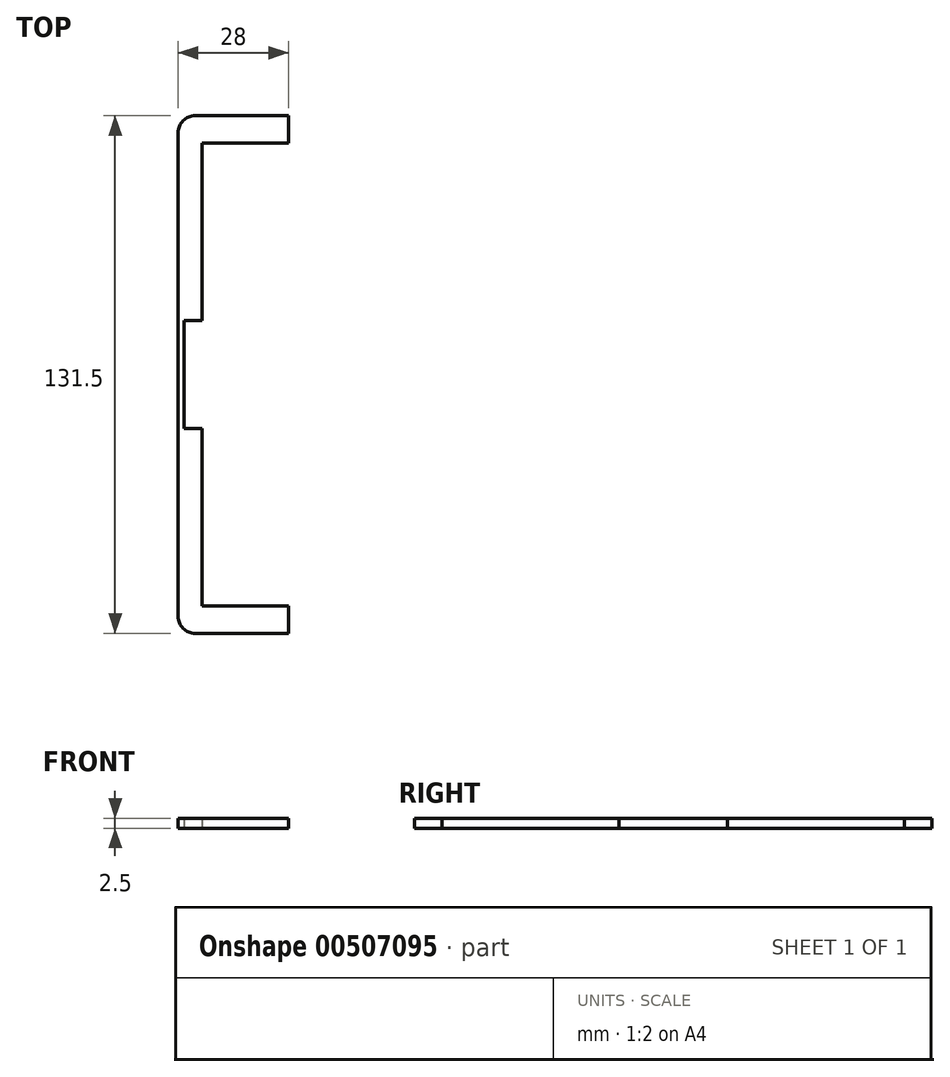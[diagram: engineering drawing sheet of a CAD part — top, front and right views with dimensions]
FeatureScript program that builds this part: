
annotation { "Feature Type Name" : "Feature", "Feature Type Description" : "" }
export const myFeature = defineFeature(function(context is Context, id is Id, definition is map)
    precondition{}
    {
        {
            var Q0;
            Q0=qCreatedBy(makeId("Top.planeOp"),FACE);
            var sketch = newSketch(context, id + "F0", { "sketchPlane" : qUnion([Q0])});
            skLineSegment(sketch, "E0", {"start": v(0, 58.75) * mm, "end": v(0, 65.75) * mm});
            skLineSegment(sketch, "E1", {"start": v(0, 65.75) * mm, "end": v(-23.68, 65.75) * mm});
            skLineSegment(sketch, "E2", {"start": v(-28, 61.43) * mm, "end": v(-28, -61.43) * mm});
            skLineSegment(sketch, "E3", {"start": v(-23.68, -65.75) * mm, "end": v(0, -65.75) * mm});
            skLineSegment(sketch, "E4", {"start": v(0, -65.75) * mm, "end": v(0, -58.75) * mm});
            skLineSegment(sketch, "E5", {"start": v(0, -58.75) * mm, "end": v(-22, -58.75) * mm});
            skLineSegment(sketch, "E6", {"start": v(-22, -58.75) * mm, "end": v(-22, -13.75) * mm});
            skLineSegment(sketch, "E7", {"start": v(-22, -13.75) * mm, "end": v(-26.5, -13.75) * mm});
            skLineSegment(sketch, "E8", {"start": v(-26.5, -13.75) * mm, "end": v(-26.5, 13.75) * mm});
            skLineSegment(sketch, "E9", {"start": v(-26.5, 13.75) * mm, "end": v(-22, 13.75) * mm});
            skLineSegment(sketch, "E10", {"start": v(-22, 13.75) * mm, "end": v(-22, 58.75) * mm});
            skLineSegment(sketch, "E11", {"start": v(-22, 58.75) * mm, "end": v(0, 58.75) * mm});
            skPoint(sketch, "E12.visualSharp", {"position": v(-28, 65.75) * mm});
            skArc(sketch, "E12.filletArc", {"start": v(-23.68, 65.75) * mm, "mid": v(-26.74, 64.49) * mm, "end": v(-28, 61.43) * mm});
            skPoint(sketch, "E13.visualSharp", {"position": v(-28, -65.75) * mm});
            skArc(sketch, "E13.filletArc", {"start": v(-28, -61.43) * mm, "mid": v(-26.74, -64.49) * mm, "end": v(-23.68, -65.75) * mm});
            skSolve(sketch);
        }
        {
            var Q0;
            Q0 = qSketchRegion(id + "F0", true);
            extrude(context, id + "F1", {"entities" : qUnion([Q0]), "depth" : 2.5 * mm});
        }
        {
            var Q0;
            Q0=makeQuery(id+"F1.opExtrude","CAP_FACE",FACE,{"disambiguationData":[OSD([sQuery(id+"F0.wireOp",EDGE,"E0"),sQuery(id+"F0.wireOp",EDGE,"E1"),sQuery(id+"F0.wireOp",EDGE,"E2"),sQuery(id+"F0.wireOp",EDGE,"E3"),sQuery(id+"F0.wireOp",EDGE,"E4"),sQuery(id+"F0.wireOp",EDGE,"E5"),sQuery(id+"F0.wireOp",EDGE,"E6"),sQuery(id+"F0.wireOp",EDGE,"E7"),sQuery(id+"F0.wireOp",EDGE,"E8"),sQuery(id+"F0.wireOp",EDGE,"E9"),sQuery(id+"F0.wireOp",EDGE,"E10"),sQuery(id+"F0.wireOp",EDGE,"E11"),sQuery(id+"F0.wireOp",EDGE,"E12.filletArc"),sQuery(id+"F0.wireOp",EDGE,"E13.filletArc")])],"isStart":false});
            var sketch = newSketch(context, id + "F2", { "sketchPlane" : qUnion([Q0])});
            skLineSegment(sketch, "E14.0", {"start": v(-22, 58.75) * mm, "end": v(0, 58.75) * mm});
            skLineSegment(sketch, "E15.0", {"start": v(-22, 13.75) * mm, "end": v(-22, 58.75) * mm});
            skLineSegment(sketch, "E16.0", {"start": v(-28, 61.43) * mm, "end": v(-28, -61.43) * mm});
            skLineSegment(sketch, "E17.0", {"start": v(-26.5, -13.75) * mm, "end": v(-26.5, 13.75) * mm});
            skPoint(sketch, "E18.0", {"position": v(-24.25, 13.75) * mm});
            skLineSegment(sketch, "E19.0", {"start": v(-26.5, 13.75) * mm, "end": v(-22, 13.75) * mm});
            skLineSegment(sketch, "E20.0", {"start": v(-22, -13.75) * mm, "end": v(-26.5, -13.75) * mm});
            skLineSegment(sketch, "E21.0", {"start": v(-22, -58.75) * mm, "end": v(-22, -13.75) * mm});
            skLineSegment(sketch, "E22.0", {"start": v(0, -58.75) * mm, "end": v(-22, -58.75) * mm});
            skLineSegment(sketch, "E23.0", {"start": v(0, -65.75) * mm, "end": v(0, -58.75) * mm});
            skLineSegment(sketch, "E24.0", {"start": v(0, 58.75) * mm, "end": v(0, 65.75) * mm});
            skLineSegment(sketch, "E25", {"start": v(0, 58.75) * mm, "end": v(0, 60.75) * mm});
            skLineSegment(sketch, "E26", {"start": v(0, 60.75) * mm, "end": v(-24, 60.75) * mm});
            skLineSegment(sketch, "E27", {"start": v(-24, 60.75) * mm, "end": v(-24, 15.75) * mm});
            skLineSegment(sketch, "E28", {"start": v(-24, 15.75) * mm, "end": v(-28, 15.75) * mm});
            skLineSegment(sketch, "E29", {"start": v(-28, 15.75) * mm, "end": v(-28, -15.75) * mm});
            skLineSegment(sketch, "E30", {"start": v(-28, -15.75) * mm, "end": v(-24, -15.75) * mm});
            skLineSegment(sketch, "E31", {"start": v(-24, -15.75) * mm, "end": v(-24, -60.75) * mm});
            skLineSegment(sketch, "E32", {"start": v(-24, -60.75) * mm, "end": v(0, -60.75) * mm});
            skLineSegment(sketch, "E33", {"start": v(0, -60.75) * mm, "end": v(0, -58.75) * mm});
            skLineSegment(sketch, "E34", {"start": v(-22, -58.75) * mm, "end": v(0, -58.75) * mm});
            skSolve(sketch);
        }
        {
            var Q0;
            Q0=qCreatedBy(makeId("Top.planeOp"),FACE);
            cPlane(context, id + "F3", {"entities" : qUnion([Q0]), "cplaneType" : CPlaneType.OFFSET, "offset" : 20 * mm, "width" : 150 * mm, "height" : 150 * mm});
        }
    });
